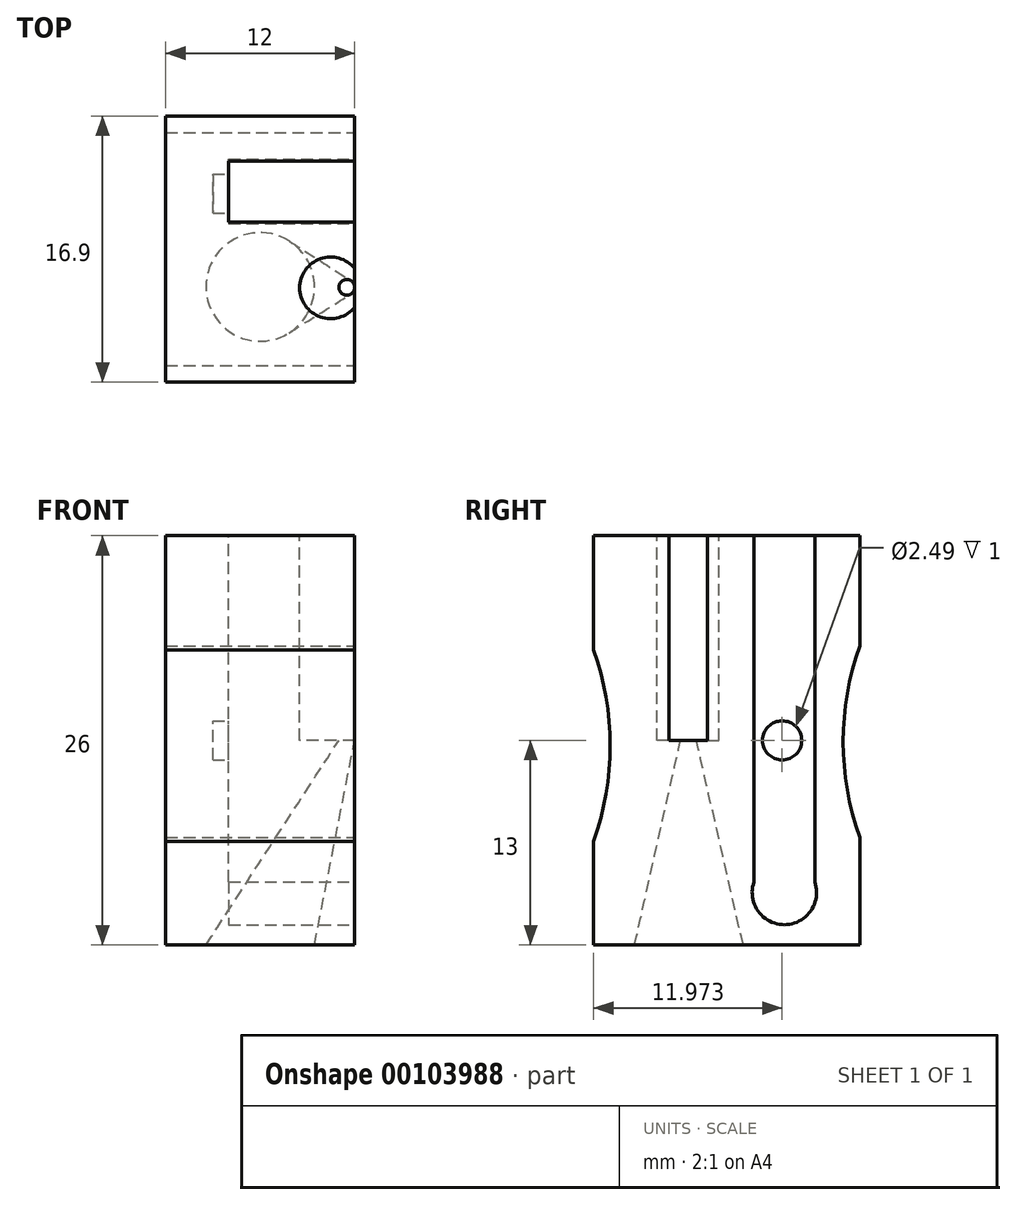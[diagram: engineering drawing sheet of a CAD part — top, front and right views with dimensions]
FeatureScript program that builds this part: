
annotation { "Feature Type Name" : "Feature", "Feature Type Description" : "" }
export const myFeature = defineFeature(function(context is Context, id is Id, definition is map)
    precondition{}
    {
        {
            var Q0;
            Q0=qCreatedBy(makeId("Right.planeOp"),FACE);
            var sketch = newSketch(context, id + "F0", { "sketchPlane" : qUnion([Q0])});
            skLineSegment(sketch, "E0.bottom", {"start": v(-8.45, 13) * mm, "end": v(8.45, 13) * mm});
            skLineSegment(sketch, "E0.top", {"start": v(-8.45, -13) * mm, "end": v(8.45, -13) * mm});
            skLineSegment(sketch, "E0.left", {"start": v(-8.45, 13) * mm, "end": v(-8.45, -13) * mm});
            skLineSegment(sketch, "E0.right", {"start": v(8.45, 13) * mm, "end": v(8.45, -13) * mm});
            skPoint(sketch, "E0.middle", {"position": v(0, 0) * mm});
            skSolve(sketch);
        }
        {
            var Q0;
            Q0 = qSketchRegion(id + "F0", true);
            extrude(context, id + "F1", {"entities" : qUnion([Q0]), "endBound" : BoundingType.SYMMETRIC, "depth" : 12 * mm});
        }
        {
            var Q0;
            Q0=qCreatedBy(makeId("Top.planeOp"),FACE);
            cPlane(context, id + "F2", {"entities" : qUnion([Q0]), "cplaneType" : CPlaneType.OFFSET, "offset" : 13 * mm, "width" : 150 * mm, "height" : 150 * mm});
        }
        {
            var Q0;
            Q0=qCreatedBy(id+"F2.planeOp",FACE);
            var sketch = newSketch(context, id + "F3", { "sketchPlane" : qUnion([Q0])});
            skArc(sketch, "E1", {"start": v(6, -1.23) * mm, "mid": v(2.5, -2.45) * mm, "end": v(6, -3.68) * mm});
            skLineSegment(sketch, "E2", {"start": v(6, -1.23) * mm, "end": v(6, -3.68) * mm});
            skSolve(sketch);
        }
        {
            var Q0;
            Q0 = qSketchRegion(id + "F3", true);
            extrude(context, id + "F4", {"entities" : qUnion([Q0]), "operationType" : NewBodyOperationType.REMOVE, "oppositeDirection" : true, "depth" : 13 * mm});
        }
        {
            var Q0;
            Q0=qCreatedBy(makeId("Top.planeOp"),FACE);
            var sketch = newSketch(context, id + "F5", { "sketchPlane" : qUnion([Q0])});
            skCircle(sketch, "E3", {"center": v(5.5, -2.42) * mm, "radius": 0.5 * mm});
            skSolve(sketch);
        }
        {
            var Q0;
            Q0=qCreatedBy(makeId("Top.planeOp"),FACE);
            cPlane(context, id + "F6", {"entities" : qUnion([Q0]), "cplaneType" : CPlaneType.OFFSET, "offset" : 13 * mm, "oppositeDirection" : true, "width" : 150 * mm, "height" : 150 * mm});
        }
        {
            var Q0;
            Q0=qCreatedBy(id+"F6.planeOp",FACE);
            var sketch = newSketch(context, id + "F7", { "sketchPlane" : qUnion([Q0])});
            skCircle(sketch, "E4", {"center": v(0, -2.4) * mm, "radius": 3.45 * mm});
            skSolve(sketch);
        }
        {
            var Q1;
            Q1 = qSketchRegion(id + "F5", true);
            var Q2;
            Q2 = qSketchRegion(id + "F7", true);
            loft(context, id + "F8", {"operationType" : NewBodyOperationType.REMOVE, "sheetProfilesArray" : [{ "sheetProfileEntities" : qUnion([Q1]) }, { "sheetProfileEntities" : qUnion([Q2]) }]});
        }
        {
            var Q0;
            Q0=qCreatedBy(makeId("Right.planeOp"),FACE);
            cPlane(context, id + "F9", {"entities" : qUnion([Q0]), "cplaneType" : CPlaneType.OFFSET, "offset" : 6 * mm, "width" : 150 * mm, "height" : 150 * mm});
        }
        {
            var Q0;
            Q0=qCreatedBy(id+"F9.planeOp",FACE);
            var sketch = newSketch(context, id + "F10", { "sketchPlane" : qUnion([Q0])});
            skArc(sketch, "E5", {"start": v(8.45, 6) * mm, "mid": v(7.4, -0.09) * mm, "end": v(8.45, -6.17) * mm});
            skLineSegment(sketch, "E6", {"start": v(8.45, -6.17) * mm, "end": v(8.45, 6) * mm});
            skArc(sketch, "E7", {"start": v(-8.45, -6.4) * mm, "mid": v(-7.4, -0.33) * mm, "end": v(-8.45, 5.75) * mm});
            skLineSegment(sketch, "E8", {"start": v(-8.45, -6.4) * mm, "end": v(-8.45, 5.75) * mm});
            skSolve(sketch);
        }
        {
            var Q0;
            Q0 = qSketchRegion(id + "F10", true);
            extrude(context, id + "F11", {"entities" : qUnion([Q0]), "operationType" : NewBodyOperationType.REMOVE, "endBound" : BoundingType.THROUGH_ALL, "oppositeDirection" : true, "depth" : 25 * mm});
        }
        {
            var Q0;
            Q0=qCreatedBy(id+"F9.planeOp",FACE);
            var sketch = newSketch(context, id + "F12", { "sketchPlane" : qUnion([Q0])});
            skArc(sketch, "E9", {"start": v(1.74, -8.98) * mm, "mid": v(3.66, -11.7) * mm, "end": v(5.6, -8.98) * mm});
            skLineSegment(sketch, "E10", {"start": v(1.74, -8.98) * mm, "end": v(1.74, 13) * mm});
            skLineSegment(sketch, "E11", {"start": v(5.6, -8.98) * mm, "end": v(5.6, 13) * mm});
            skLineSegment(sketch, "E12", {"start": v(1.74, 13) * mm, "end": v(5.6, 13) * mm});
            skSolve(sketch);
        }
        {
            var Q0;
            Q0 = qSketchRegion(id + "F12", true);
            extrude(context, id + "F13", {"entities" : qUnion([Q0]), "operationType" : NewBodyOperationType.REMOVE, "oppositeDirection" : true, "depth" : 8 * mm});
        }
        {
            var Q0;
            Q0=qCreatedBy(id+"F9.planeOp",FACE);
            cPlane(context, id + "F14", {"entities" : qUnion([Q0]), "cplaneType" : CPlaneType.OFFSET, "offset" : 4 * mm, "oppositeDirection" : true, "width" : 150 * mm, "height" : 150 * mm});
        }
        {
            var Q0;
            Q0=qCreatedBy(id+"F14.planeOp",FACE);
            var sketch = newSketch(context, id + "F15", { "sketchPlane" : qUnion([Q0])});
            skCircle(sketch, "E13", {"center": v(3.52, 0) * mm, "radius": 1.24 * mm});
            skSolve(sketch);
        }
        {
            var Q0;
            Q0 = qSketchRegion(id + "F15", true);
            extrude(context, id + "F16", {"entities" : qUnion([Q0]), "operationType" : NewBodyOperationType.REMOVE, "oppositeDirection" : true, "depth" : 5 * mm});
        }
    });
